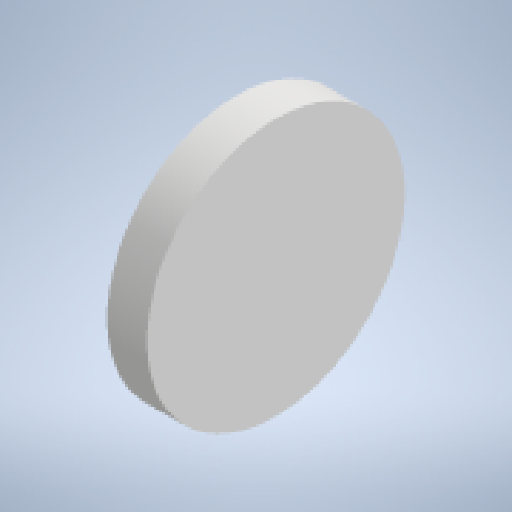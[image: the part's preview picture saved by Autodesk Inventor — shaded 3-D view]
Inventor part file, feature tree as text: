
AUTODESK INVENTOR PART (.ipt)
format: ipt  version: 2024.3 (Build 283343000, 343)  size: 140,800 bytes
history: native  units: mm
features: extrude x1, sketch x1
ambient origin geometry x8: Origin, YZ Plane, XZ Plane, XY Plane, X Axis, Y Axis, Z Axis, Center Point
bodies: Solid1 (feature_tree)
feature tree (2):
  extrude  "Extrusion1"  Depth=17.0mm TaperAngle=0.0deg
  sketch  "Sketch1"  dims[d0=110.0mm d1=17.0mm d2=0.0mm]
